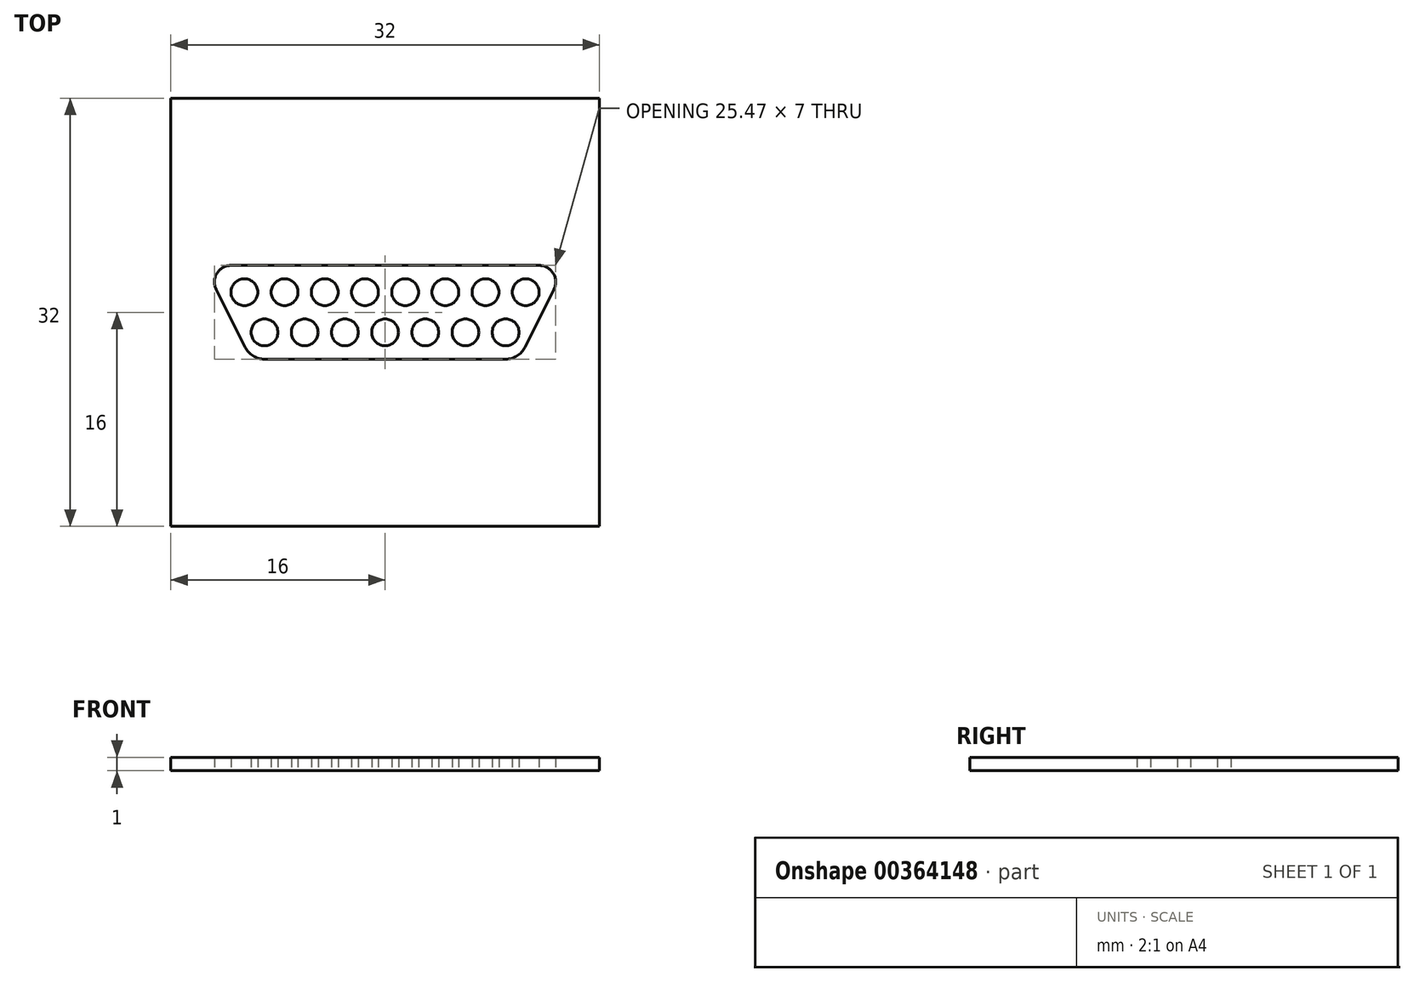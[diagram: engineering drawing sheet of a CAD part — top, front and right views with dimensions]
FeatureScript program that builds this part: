
annotation { "Feature Type Name" : "Feature", "Feature Type Description" : "" }
export const myFeature = defineFeature(function(context is Context, id is Id, definition is map)
    precondition{}
    {
        {
            var Q0;
            Q0=qCreatedBy(makeId("Top.planeOp"),FACE);
            var sketch = newSketch(context, id + "F0", { "sketchPlane" : qUnion([Q0])});
            skCircle(sketch, "E0", {"center": v(0, 0) * mm, "radius": 1 * mm});
            skCircle(sketch, "E1.1.0.0", {"center": v(3, 0) * mm, "radius": 1 * mm});
            skCircle(sketch, "E1.2.0.0", {"center": v(6, 0) * mm, "radius": 1 * mm});
            skCircle(sketch, "E1.3.0.0", {"center": v(9, 0) * mm, "radius": 1 * mm});
            skLineSegment(sketch, "E1.direction1", {"start": v(0, 0) * mm, "end": v(3, 0) * mm, "construction": true});
            skCircle(sketch, "E2.1.0.0", {"center": v(-3, 0) * mm, "radius": 1 * mm});
            skCircle(sketch, "E2.2.0.0", {"center": v(-6, 0) * mm, "radius": 1 * mm});
            skCircle(sketch, "E2.3.0.0", {"center": v(-9, 0) * mm, "radius": 1 * mm});
            skLineSegment(sketch, "E2.direction1", {"start": v(0, 0) * mm, "end": v(-3, 0) * mm, "construction": true});
            skLineSegment(sketch, "E3", {"start": v(0, 0) * mm, "end": v(0, 3) * mm});
            skLineSegment(sketch, "E4", {"start": v(0, 3) * mm, "end": v(-1.5, 3) * mm});
            skCircle(sketch, "E5", {"center": v(-1.5, 3) * mm, "radius": 1 * mm});
            skCircle(sketch, "E6.1.0.0", {"center": v(1.5, 3) * mm, "radius": 1 * mm});
            skCircle(sketch, "E6.2.0.0", {"center": v(4.5, 3) * mm, "radius": 1 * mm});
            skCircle(sketch, "E6.3.0.0", {"center": v(7.5, 3) * mm, "radius": 1 * mm});
            skCircle(sketch, "E6.4.0.0", {"center": v(10.5, 3) * mm, "radius": 1 * mm});
            skLineSegment(sketch, "E6.direction1", {"start": v(-1.5, 3) * mm, "end": v(1.5, 3) * mm, "construction": true});
            skCircle(sketch, "E7.1.0.0", {"center": v(-4.5, 3) * mm, "radius": 1 * mm});
            skCircle(sketch, "E7.2.0.0", {"center": v(-7.5, 3) * mm, "radius": 1 * mm});
            skCircle(sketch, "E7.3.0.0", {"center": v(-10.5, 3) * mm, "radius": 1 * mm});
            skLineSegment(sketch, "E7.direction1", {"start": v(-1.5, 3) * mm, "end": v(-4.5, 3) * mm, "construction": true});
            skLineSegment(sketch, "E8", {"start": v(-9, -2) * mm, "end": v(9, -2) * mm});
            skLineSegment(sketch, "E9", {"start": v(-12.5, 3) * mm, "end": v(-11, 0) * mm});
            skLineSegment(sketch, "E10", {"start": v(-10.5, 5) * mm, "end": v(11.5, 5) * mm});
            skLineSegment(sketch, "E11", {"start": v(-12.5, 3) * mm, "end": v(-10.45, -1.1) * mm});
            skLineSegment(sketch, "E12", {"start": v(-10.45, -1.1) * mm, "end": v(-12.6, 3.21) * mm});
            skLineSegment(sketch, "E13", {"start": v(-10.5, 5) * mm, "end": v(-11.5, 5) * mm});
            skLineSegment(sketch, "E14", {"start": v(12.5, 3) * mm, "end": v(11, 0) * mm});
            skLineSegment(sketch, "E15", {"start": v(11, 0) * mm, "end": v(12.6, 3.21) * mm});
            skLineSegment(sketch, "E16", {"start": v(12.6, 3.21) * mm, "end": v(10.45, -1.1) * mm});
            skArc(sketch, "E17", {"start": v(-11.5, 5) * mm, "mid": v(-12.55, 4.41) * mm, "end": v(-12.6, 3.21) * mm});
            skArc(sketch, "E18", {"start": v(12.6, 3.21) * mm, "mid": v(12.55, 4.41) * mm, "end": v(11.5, 5) * mm});
            skArc(sketch, "E19", {"start": v(-10.45, -1.1) * mm, "mid": v(-9.85, -1.76) * mm, "end": v(-9, -2) * mm});
            skArc(sketch, "E20", {"start": v(9, -2) * mm, "mid": v(9.85, -1.76) * mm, "end": v(10.45, -1.1) * mm});
            skLineSegment(sketch, "E21.bottom", {"start": v(16, -14.5) * mm, "end": v(-16, -14.5) * mm});
            skLineSegment(sketch, "E21.top", {"start": v(16, 17.5) * mm, "end": v(-16, 17.5) * mm});
            skLineSegment(sketch, "E21.left", {"start": v(16, -14.5) * mm, "end": v(16, 17.5) * mm});
            skLineSegment(sketch, "E21.right", {"start": v(-16, -14.5) * mm, "end": v(-16, 17.5) * mm});
            skPoint(sketch, "E21.middle", {"position": v(0, 1.5) * mm});
            skSolve(sketch);
        }
        {
            var Q0;
            Q0=makeQuery(id+"F0.imprint","IMPRINT",FACE,{"disambiguationData":[TD([[makeQuery(id+"F0.imprint","IMPRINT",EDGE,{"derivedFrom":sQuery(id+"F0.wireOp",EDGE,"E7.3.0.0")}),1.0]])]});
            var Q1;
            Q1=makeQuery(id+"F0.imprint","IMPRINT",FACE,{"disambiguationData":[TD([[makeQuery(id+"F0.imprint","IMPRINT",EDGE,{"derivedFrom":sQuery(id+"F0.wireOp",EDGE,"E7.2.0.0")}),1.0]])]});
            var Q2;
            Q2=makeQuery(id+"F0.imprint","IMPRINT",FACE,{"disambiguationData":[TD([[makeQuery(id+"F0.imprint","IMPRINT",EDGE,{"derivedFrom":sQuery(id+"F0.wireOp",EDGE,"E7.1.0.0")}),1.0]])]});
            var Q3;
            Q3=makeQuery(id+"F0.imprint","IMPRINT",FACE,{"disambiguationData":[TD([[makeQuery(id+"F0.imprint","IMPRINT",EDGE,{"derivedFrom":sQuery(id+"F0.wireOp",EDGE,"E5")}),1.0]])]});
            var Q4;
            Q4=makeQuery(id+"F0.imprint","IMPRINT",FACE,{"disambiguationData":[TD([[makeQuery(id+"F0.imprint","IMPRINT",EDGE,{"derivedFrom":sQuery(id+"F0.wireOp",EDGE,"E6.1.0.0")}),1.0]])]});
            var Q5;
            Q5=makeQuery(id+"F0.imprint","IMPRINT",FACE,{"disambiguationData":[TD([[makeQuery(id+"F0.imprint","IMPRINT",EDGE,{"derivedFrom":sQuery(id+"F0.wireOp",EDGE,"E6.2.0.0")}),1.0]])]});
            var Q6;
            Q6=makeQuery(id+"F0.imprint","IMPRINT",FACE,{"disambiguationData":[TD([[makeQuery(id+"F0.imprint","IMPRINT",EDGE,{"derivedFrom":sQuery(id+"F0.wireOp",EDGE,"E6.3.0.0")}),1.0]])]});
            var Q7;
            Q7=makeQuery(id+"F0.imprint","IMPRINT",FACE,{"disambiguationData":[TD([[makeQuery(id+"F0.imprint","IMPRINT",EDGE,{"derivedFrom":sQuery(id+"F0.wireOp",EDGE,"E6.4.0.0")}),1.0]])]});
            var Q8;
            Q8=makeQuery(id+"F0.imprint","IMPRINT",FACE,{"disambiguationData":[TD([[makeQuery(id+"F0.imprint","IMPRINT",EDGE,{"derivedFrom":sQuery(id+"F0.wireOp",EDGE,"E2.3.0.0")}),1.0]])]});
            var Q9;
            Q9=makeQuery(id+"F0.imprint","IMPRINT",FACE,{"disambiguationData":[TD([[makeQuery(id+"F0.imprint","IMPRINT",EDGE,{"derivedFrom":sQuery(id+"F0.wireOp",EDGE,"E2.2.0.0")}),1.0]])]});
            var Q10;
            Q10=makeQuery(id+"F0.imprint","IMPRINT",FACE,{"disambiguationData":[TD([[makeQuery(id+"F0.imprint","IMPRINT",EDGE,{"derivedFrom":sQuery(id+"F0.wireOp",EDGE,"E2.1.0.0")}),1.0]])]});
            var Q11;
            Q11=makeQuery(id+"F0.imprint","IMPRINT",FACE,{"disambiguationData":[TD([[makeQuery(id+"F0.imprint","IMPRINT",EDGE,{"derivedFrom":sQuery(id+"F0.wireOp",EDGE,"E0")}),1.0]])]});
            var Q12;
            Q12=makeQuery(id+"F0.imprint","IMPRINT",FACE,{"disambiguationData":[TD([[makeQuery(id+"F0.imprint","IMPRINT",EDGE,{"derivedFrom":sQuery(id+"F0.wireOp",EDGE,"E1.1.0.0")}),1.0]])]});
            var Q13;
            Q13=makeQuery(id+"F0.imprint","IMPRINT",FACE,{"disambiguationData":[TD([[makeQuery(id+"F0.imprint","IMPRINT",EDGE,{"derivedFrom":sQuery(id+"F0.wireOp",EDGE,"E1.2.0.0")}),1.0]])]});
            var Q14;
            Q14=makeQuery(id+"F0.imprint","IMPRINT",FACE,{"disambiguationData":[TD([[makeQuery(id+"F0.imprint","IMPRINT",EDGE,{"derivedFrom":sQuery(id+"F0.wireOp",EDGE,"E1.3.0.0")}),1.0]])]});
            extrude(context, id + "F1", {"entities" : qUnion([Q0, Q1, Q2, Q3, Q4, Q5, Q6, Q7, Q8, Q9, Q10, Q11, Q12, Q13, Q14]), "depth" : 1 * mm});
        }
        {
            var Q0;
            Q0=makeQuery(id+"F0.imprint","IMPRINT",FACE,{"disambiguationData":[TD([[makeQuery(id+"F0.imprint","IMPRINT",EDGE,{"derivedFrom":sQuery(id+"F0.wireOp",EDGE,"E8")}),-1.0]])]});
            extrude(context, id + "F2", {"entities" : qUnion([Q0]), "depth" : 1 * mm});
        }
    });
